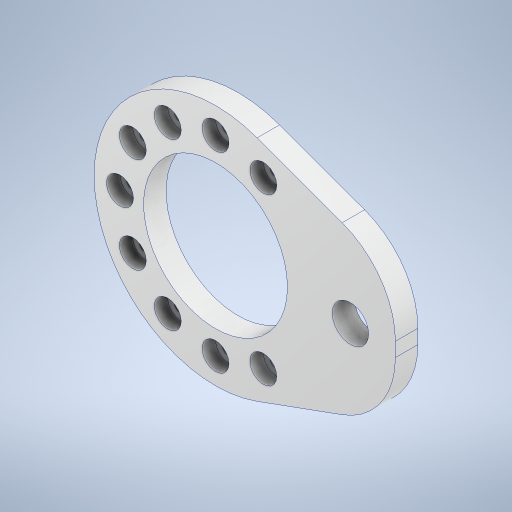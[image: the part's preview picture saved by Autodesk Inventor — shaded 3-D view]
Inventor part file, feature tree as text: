
AUTODESK INVENTOR PART (.ipt)
format: ipt  version: 2024.3 (Build 283343000, 343)  size: 479,744 bytes
history: native  units: mm
features: sketch x11, extrude x7, hole x4, other x2, fillet x1
ambient origin geometry x8: Origin, YZ Plane, XZ Plane, XY Plane, X Axis, Y Axis, Z Axis, Center Point
bodies: Body1 (feature_tree)
feature tree (25):
  other  "ソリッド1"
  other  "作業平面1"
  extrude  "押し出し9"  Depth=50.0mm
  extrude  "押し出し10"  Depth=8.1mm
  extrude  "押し出し11"  Depth=30.0mm
  hole  "穴5"  [1 undecoded]
  hole  "穴6"  [1 undecoded]
  extrude  "押し出し12"  Depth=25.0mm
  hole  "穴7"  [1 undecoded]
  extrude  "押し出し13"  Depth=5.0mm TaperAngle=0.0deg
  hole  "穴8"  [1 undecoded]
  extrude  "押し出し14"  Depth=2.0mm TaperAngle=0.0deg
  extrude  "押し出し15"  Depth=34.0mm
  fillet  "フィレット10"  Radius=3.490659mm
  sketch  "スケッチ14"
  sketch  "スケッチ15"
  sketch  "スケッチ16"
  sketch  "スケッチ17"
  sketch  "スケッチ18"
  sketch  "スケッチ19"
  sketch  "スケッチ20"
  sketch  "スケッチ21"
  sketch  "スケッチ22"
  sketch  "スケッチ23"
  sketch  "スケッチ24"
note: 4 required parameter values undecoded (feature->parameter linkage not recoverable at this tier; creation-order binding heuristic only, values carry confidence <= 0.55)
